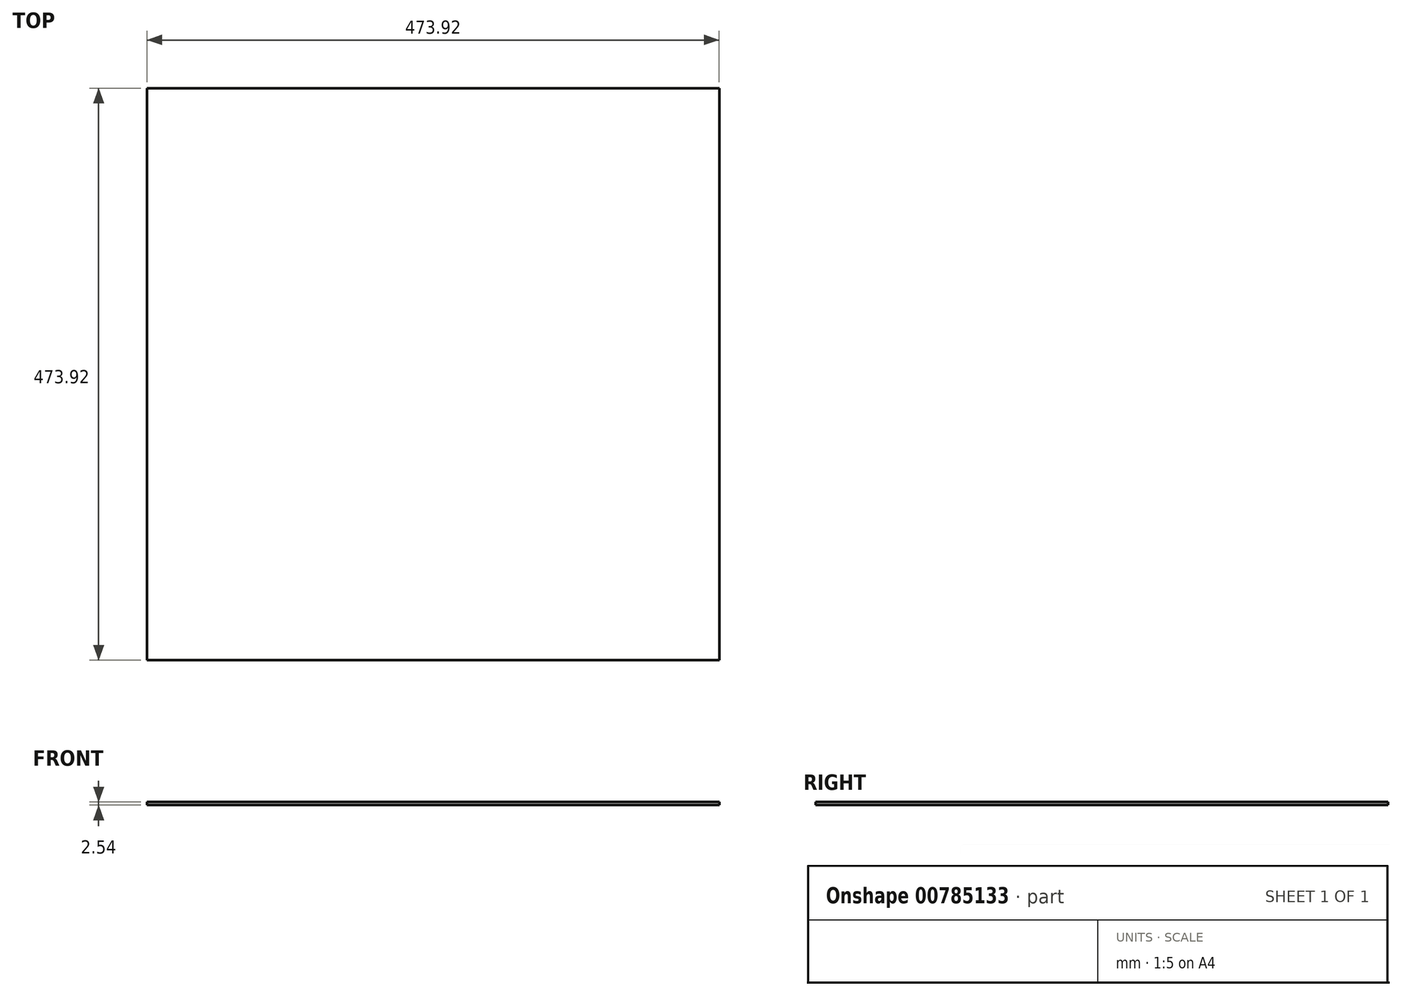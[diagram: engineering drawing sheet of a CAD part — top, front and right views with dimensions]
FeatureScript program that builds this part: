
annotation { "Feature Type Name" : "Feature", "Feature Type Description" : "" }
export const myFeature = defineFeature(function(context is Context, id is Id, definition is map)
    precondition{}
    {
        {
            var Q0;
            Q0=qCreatedBy(makeId("Top.planeOp"),FACE);
            var sketch = newSketch(context, id + "F0", { "sketchPlane" : qUnion([Q0])});
            skLineSegment(sketch, "E0.bottom", {"start": v(236.96, -236.96) * mm, "end": v(-236.96, -236.96) * mm});
            skLineSegment(sketch, "E0.top", {"start": v(236.96, 236.96) * mm, "end": v(-236.96, 236.96) * mm});
            skLineSegment(sketch, "E0.left", {"start": v(236.96, -236.96) * mm, "end": v(236.96, 236.96) * mm});
            skLineSegment(sketch, "E0.right", {"start": v(-236.96, -236.96) * mm, "end": v(-236.96, 236.96) * mm});
            skPoint(sketch, "E0.middle", {"position": v(0, 0) * mm});
            skSolve(sketch);
        }
        {
            var Q0;
            Q0=makeQuery(id+"F0.imprint","IMPRINT",FACE,{"disambiguationData":[TD([[makeQuery(id+"F0.imprint","IMPRINT",EDGE,{"derivedFrom":sQuery(id+"F0.wireOp",EDGE,"E0.bottom")}),-1.0]])]});
            extrude(context, id + "F1", {"entities" : qUnion([Q0]), "depth" : 2.54 * mm, "offsetDistance" : 25.4 * mm});
        }
    });
